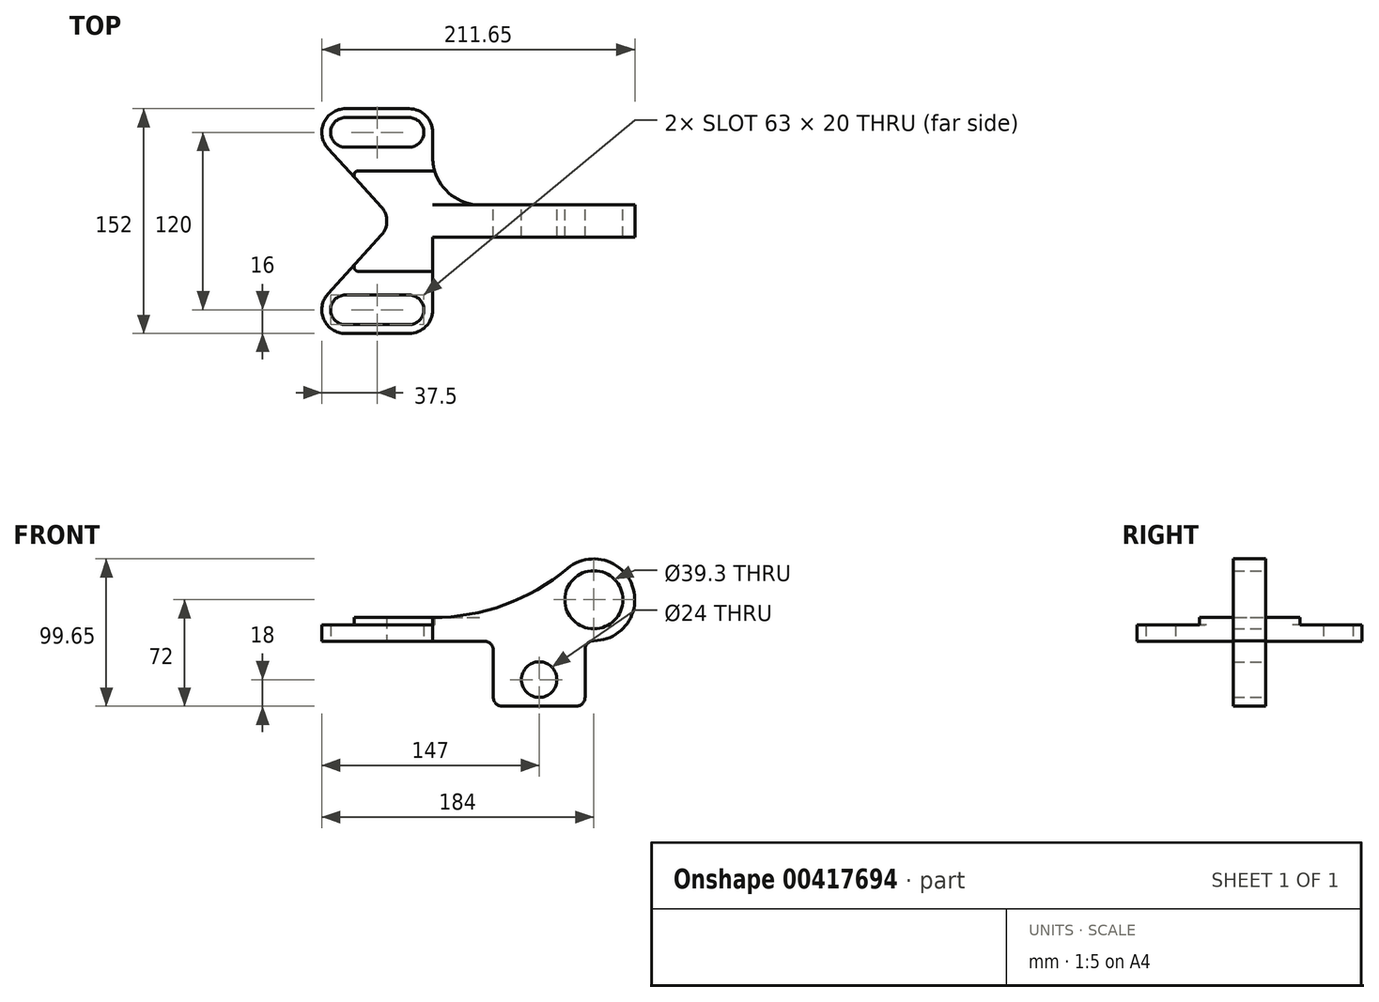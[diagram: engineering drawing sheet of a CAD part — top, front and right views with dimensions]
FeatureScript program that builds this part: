
annotation { "Feature Type Name" : "Feature", "Feature Type Description" : "" }
export const myFeature = defineFeature(function(context is Context, id is Id, definition is map)
    precondition{}
    {
        {
            var Q0;
            Q0=qCreatedBy(makeId("Top.planeOp"),FACE);
            var sketch = newSketch(context, id + "F0", { "sketchPlane" : qUnion([Q0])});
            skLineSegment(sketch, "E0.bottom", {"start": v(-59, 70) * mm, "end": v(-16, 70) * mm});
            skLineSegment(sketch, "E0.top", {"start": v(-59, 50) * mm, "end": v(-16, 50) * mm});
            skLineSegment(sketch, "E0.left", {"start": v(-59, 70) * mm, "end": v(-59, 50) * mm, "construction": true});
            skLineSegment(sketch, "E0.right", {"start": v(-16, 70) * mm, "end": v(-16, 50) * mm, "construction": true});
            skArc(sketch, "E1", {"start": v(-59, 70) * mm, "mid": v(-69, 60) * mm, "end": v(-59, 50) * mm});
            skArc(sketch, "E2", {"start": v(-16, 50) * mm, "mid": v(-6, 60) * mm, "end": v(-16, 70) * mm});
            skArc(sketch, "E3.0", {"start": v(-59, 76) * mm, "mid": v(-73.63, 66.47) * mm, "end": v(-70.84, 49.24) * mm});
            skLineSegment(sketch, "E3.1", {"start": v(-59, 76) * mm, "end": v(-16, 76) * mm});
            skArc(sketch, "E3.2", {"start": v(-16, 44) * mm, "mid": v(-4.69, 48.69) * mm, "end": v(0, 60) * mm, "construction": true});
            skLineSegment(sketch, "E3.3", {"start": v(-59, 44) * mm, "end": v(-16, 44) * mm, "construction": true});
            skLineSegment(sketch, "E4", {"start": v(-70.84, 49.24) * mm, "end": v(-34.64, 9.42) * mm});
            skLineSegment(sketch, "E5", {"start": v(0, 60) * mm, "end": v(0, 0) * mm});
            skArc(sketch, "E6", {"start": v(-31, 0) * mm, "mid": v(-31.94, 5.05) * mm, "end": v(-34.64, 9.42) * mm});
            skArc(sketch, "E7", {"start": v(-70.84, 49.24) * mm, "mid": v(-65.47, 45.37) * mm, "end": v(-59, 44) * mm, "construction": true});
            skArc(sketch, "E8", {"start": v(0, 60) * mm, "mid": v(-4.69, 71.31) * mm, "end": v(-16, 76) * mm});
            skArc(sketch, "E9.MirrorCS", {"start": v(-31, 0) * mm, "mid": v(-31.94, -5.05) * mm, "end": v(-34.64, -9.42) * mm});
            skLineSegment(sketch, "E10.MirrorCS", {"start": v(-70.84, -49.24) * mm, "end": v(-34.64, -9.42) * mm});
            skArc(sketch, "E11.MirrorCS", {"start": v(-59, -76) * mm, "mid": v(-73.63, -66.47) * mm, "end": v(-70.84, -49.24) * mm});
            skLineSegment(sketch, "E12.MirrorCS", {"start": v(-59, -76) * mm, "end": v(-16, -76) * mm});
            skArc(sketch, "E13.MirrorCS", {"start": v(0, -60) * mm, "mid": v(-4.69, -71.31) * mm, "end": v(-16, -76) * mm});
            skLineSegment(sketch, "E14.MirrorCS", {"start": v(0, -60) * mm, "end": v(0, 0) * mm});
            skArc(sketch, "E15.MirrorCS", {"start": v(-16, -50) * mm, "mid": v(-6, -60) * mm, "end": v(-16, -70) * mm});
            skLineSegment(sketch, "E16.MirrorCS", {"start": v(-59, -50) * mm, "end": v(-16, -50) * mm});
            skArc(sketch, "E17.MirrorCS", {"start": v(-59, -70) * mm, "mid": v(-69, -60) * mm, "end": v(-59, -50) * mm});
            skLineSegment(sketch, "E18.MirrorCS", {"start": v(-59, -70) * mm, "end": v(-16, -70) * mm});
            skSolve(sketch);
        }
        {
            var Q0;
            Q0=makeQuery(id+"F0.imprint","IMPRINT",FACE,{"disambiguationData":[TD([[makeQuery(id+"F0.imprint","IMPRINT",EDGE,{"derivedFrom":sQuery(id+"F0.wireOp",EDGE,"E0.bottom")}),1.0]])]});
            extrude(context, id + "F1", {"entities" : qUnion([Q0]), "depth" : 11 * mm});
        }
        {
            var Q0;
            Q0=makeQuery(id+"F1.opExtrude","CAP_FACE",FACE,{"disambiguationData":[OSD([sQuery(id+"F0.wireOp",EDGE,"E0.bottom"),sQuery(id+"F0.wireOp",EDGE,"E0.top"),sQuery(id+"F0.wireOp",EDGE,"E1"),sQuery(id+"F0.wireOp",EDGE,"E2"),sQuery(id+"F0.wireOp",EDGE,"E3.0"),sQuery(id+"F0.wireOp",EDGE,"E3.1"),sQuery(id+"F0.wireOp",EDGE,"E4"),sQuery(id+"F0.wireOp",EDGE,"E5"),sQuery(id+"F0.wireOp",EDGE,"E6"),sQuery(id+"F0.wireOp",EDGE,"E8"),sQuery(id+"F0.wireOp",EDGE,"E9.MirrorCS"),sQuery(id+"F0.wireOp",EDGE,"E10.MirrorCS"),sQuery(id+"F0.wireOp",EDGE,"E11.MirrorCS"),sQuery(id+"F0.wireOp",EDGE,"E12.MirrorCS"),sQuery(id+"F0.wireOp",EDGE,"E13.MirrorCS"),sQuery(id+"F0.wireOp",EDGE,"E14.MirrorCS"),sQuery(id+"F0.wireOp",EDGE,"E15.MirrorCS"),sQuery(id+"F0.wireOp",EDGE,"E16.MirrorCS"),sQuery(id+"F0.wireOp",EDGE,"E17.MirrorCS"),sQuery(id+"F0.wireOp",EDGE,"E18.MirrorCS")])],"isStart":false});
            var sketch = newSketch(context, id + "F2", { "sketchPlane" : qUnion([Q0])});
            skLineSegment(sketch, "E19.0", {"start": v(-52.43, 28.98) * mm, "end": v(-34.64, 9.42) * mm});
            skArc(sketch, "E19.1", {"start": v(-34.64, -9.42) * mm, "mid": v(-31, 0) * mm, "end": v(-34.64, 9.42) * mm});
            skLineSegment(sketch, "E19.2", {"start": v(-52.43, -28.98) * mm, "end": v(-34.64, -9.42) * mm});
            skLineSegment(sketch, "E19.3", {"start": v(0, 34) * mm, "end": v(0, -34) * mm});
            skLineSegment(sketch, "E20", {"start": v(-50.2, 34) * mm, "end": v(0, 34) * mm});
            skLineSegment(sketch, "E21.MirrorCS", {"start": v(-50.2, -34) * mm, "end": v(0, -34) * mm});
            skPoint(sketch, "E22.orphan", {"position": v(-70.84, 49.24) * mm});
            skPoint(sketch, "E23.orphan", {"position": v(0, 60) * mm});
            skPoint(sketch, "E24.orphan", {"position": v(0, -60) * mm});
            skPoint(sketch, "E25.orphan", {"position": v(-70.84, -49.24) * mm});
            skPoint(sketch, "E26.visualSharp", {"position": v(-56.99, 34) * mm});
            skArc(sketch, "E26.filletArc", {"start": v(-50.2, 34) * mm, "mid": v(-52.95, 32.21) * mm, "end": v(-52.43, 28.98) * mm});
            skPoint(sketch, "E27.visualSharp", {"position": v(-56.99, -34) * mm});
            skArc(sketch, "E27.filletArc", {"start": v(-52.43, -28.98) * mm, "mid": v(-52.95, -32.21) * mm, "end": v(-50.2, -34) * mm});
            skSolve(sketch);
        }
        {
            var Q0;
            Q0=makeQuery(id+"F2.imprint","IMPRINT",FACE,{"disambiguationData":[TD([[makeQuery(id+"F2.imprint","IMPRINT",EDGE,{"derivedFrom":sQuery(id+"F2.wireOp",EDGE,"E19.0")}),1.0]])]});
            extrude(context, id + "F3", {"entities" : qUnion([Q0]), "operationType" : NewBodyOperationType.ADD, "depth" : 5 * mm});
        }
        {
            var Q0;
            Q0=qCreatedBy(makeId("Front.planeOp"),FACE);
            var sketch = newSketch(context, id + "F4", { "sketchPlane" : qUnion([Q0])});
            skLineSegment(sketch, "E28", {"start": v(0, 0) * mm, "end": v(0, 16) * mm});
            skCircle(sketch, "E29", {"center": v(109, 28) * mm, "radius": 19.65 * mm});
            skCircle(sketch, "E30", {"center": v(72, -26) * mm, "radius": 12 * mm});
            skArc(sketch, "E31", {"start": v(0, 16) * mm, "mid": v(48.54, 24.55) * mm, "end": v(91.24, 49.19) * mm});
            skLineSegment(sketch, "E32", {"start": v(103, -5.65) * mm, "end": v(103, -38) * mm});
            skLineSegment(sketch, "E33", {"start": v(97, -44) * mm, "end": v(47, -44) * mm});
            skLineSegment(sketch, "E34", {"start": v(41, -38) * mm, "end": v(41, -6) * mm});
            skLineSegment(sketch, "E35", {"start": v(35, 0) * mm, "end": v(0, 0) * mm});
            skArc(sketch, "E36", {"start": v(109, 0.35) * mm, "mid": v(104.76, -1.4) * mm, "end": v(103, -5.65) * mm});
            skPoint(sketch, "E37.visualSharp", {"position": v(41, 0) * mm});
            skArc(sketch, "E37.filletArc", {"start": v(41, -6) * mm, "mid": v(39.24, -1.76) * mm, "end": v(35, 0) * mm});
            skPoint(sketch, "E38.visualSharp", {"position": v(41, -44) * mm});
            skArc(sketch, "E38.filletArc", {"start": v(41, -38) * mm, "mid": v(42.76, -42.24) * mm, "end": v(47, -44) * mm});
            skPoint(sketch, "E39.visualSharp", {"position": v(103, -44) * mm});
            skArc(sketch, "E39.filletArc", {"start": v(97, -44) * mm, "mid": v(101.24, -42.24) * mm, "end": v(103, -38) * mm});
            skArc(sketch, "E40", {"start": v(91.24, 49.19) * mm, "mid": v(83.02, 18.55) * mm, "end": v(109, 0.35) * mm, "construction": true});
            skArc(sketch, "E41", {"start": v(109, 0.35) * mm, "mid": v(134.98, 37.45) * mm, "end": v(91.24, 49.19) * mm});
            skLineSegment(sketch, "E42.0", {"start": v(-50.2, 16) * mm, "end": v(0, 16) * mm, "construction": true});
            skSolve(sketch);
        }
        {
            var Q0;
            Q0=makeQuery(id+"F4.imprint","IMPRINT",FACE,{"disambiguationData":[TD([[makeQuery(id+"F4.imprint","IMPRINT",EDGE,{"derivedFrom":sQuery(id+"F4.wireOp",EDGE,"E28")}),-1.0]])]});
            extrude(context, id + "F5", {"entities" : qUnion([Q0]), "operationType" : NewBodyOperationType.ADD, "endBound" : BoundingType.SYMMETRIC, "depth" : 22 * mm});
        }
        {
            var Q0;
            Q0=qCreatedBy(makeId("Top.planeOp"),FACE);
            var sketch = newSketch(context, id + "F6", { "sketchPlane" : qUnion([Q0])});
            skArc(sketch, "E43", {"start": v(0, 43) * mm, "mid": v(9.37, 20.37) * mm, "end": v(32, 11) * mm});
            skLineSegment(sketch, "E44.0", {"start": v(0, 34) * mm, "end": v(0, 11) * mm});
            skLineSegment(sketch, "E44.1", {"start": v(0, 11) * mm, "end": v(32, 11) * mm});
            skLineSegment(sketch, "E44.2", {"start": v(0, 43) * mm, "end": v(0, 34) * mm});
            skPoint(sketch, "E45.orphan", {"position": v(0, 60) * mm});
            skPoint(sketch, "E46.orphan", {"position": v(91.24, 11) * mm});
            skArc(sketch, "E47.MirrorCS", {"start": v(0, -43) * mm, "mid": v(9.37, -20.37) * mm, "end": v(32, -11) * mm});
            skLineSegment(sketch, "E48.MirrorCS", {"start": v(0, -11) * mm, "end": v(32, -11) * mm});
            skLineSegment(sketch, "E49.MirrorCS", {"start": v(0, -34) * mm, "end": v(0, -11) * mm});
            skLineSegment(sketch, "E50.MirrorCS", {"start": v(0, -43) * mm, "end": v(0, -34) * mm});
            skSolve(sketch);
        }
        {
            var Q0;
            Q0=makeQuery(id+"F6.imprint","IMPRINT",FACE,{"disambiguationData":[TD([[makeQuery(id+"F6.imprint","IMPRINT",EDGE,{"derivedFrom":sQuery(id+"F6.wireOp",EDGE,"E43")}),-1.0]])]});
            var Q1;
            Q1=makeQuery(id+"F6.imprint","IMPRINT",FACE,{"disambiguationData":[TD([[makeQuery(id+"F6.imprint","IMPRINT",EDGE,{"derivedFrom":sQuery(id+"F6.wireOp",EDGE,"E47.MirrorCS")}),1.0]])]});
            var Q2;
            Q2=makeQuery(id+"F3.opExtrude","CAP_FACE",FACE,{"disambiguationData":[OSD([sQuery(id+"F2.wireOp",EDGE,"E19.0"),sQuery(id+"F2.wireOp",EDGE,"E19.1"),sQuery(id+"F2.wireOp",EDGE,"E19.2"),sQuery(id+"F2.wireOp",EDGE,"E19.3"),sQuery(id+"F2.wireOp",EDGE,"E20"),sQuery(id+"F2.wireOp",EDGE,"E21.MirrorCS"),sQuery(id+"F2.wireOp",EDGE,"E26.filletArc"),sQuery(id+"F2.wireOp",EDGE,"E27.filletArc")])],"isStart":false});
            extrude(context, id + "F7", {"entities" : qUnion([Q0, Q1]), "operationType" : NewBodyOperationType.ADD, "endBound" : BoundingType.UP_TO_SURFACE, "endBoundEntityFace" : qUnion([Q2]), "depth" : 25 * mm});
        }
        {
            var Q0;
            Q0=qCreatedBy(makeId("Right.planeOp"),FACE);
            var sketch = newSketch(context, id + "F8", { "sketchPlane" : qUnion([Q0])});
            skLineSegment(sketch, "E51.bottom", {"start": v(43, 16) * mm, "end": v(34, 16) * mm});
            skLineSegment(sketch, "E51.top", {"start": v(43, 11) * mm, "end": v(34, 11) * mm});
            skLineSegment(sketch, "E51.left", {"start": v(43, 16) * mm, "end": v(43, 11) * mm});
            skLineSegment(sketch, "E51.right", {"start": v(34, 16) * mm, "end": v(34, 11) * mm});
            skLineSegment(sketch, "E52.MirrorCS", {"start": v(-34, 16) * mm, "end": v(-34, 11) * mm});
            skLineSegment(sketch, "E53.MirrorCS", {"start": v(-43, 16) * mm, "end": v(-43, 11) * mm});
            skLineSegment(sketch, "E54.MirrorCS", {"start": v(-43, 11) * mm, "end": v(-34, 11) * mm});
            skLineSegment(sketch, "E55.MirrorCS", {"start": v(-43, 16) * mm, "end": v(-34, 16) * mm});
            skSolve(sketch);
        }
        {
            var Q0;
            Q0=makeQuery(id+"F8.imprint","IMPRINT",FACE,{"disambiguationData":[TD([[makeQuery(id+"F8.imprint","IMPRINT",EDGE,{"derivedFrom":sQuery(id+"F8.wireOp",EDGE,"E51.bottom")}),1.0]])]});
            var Q1;
            Q1=makeQuery(id+"F8.imprint","IMPRINT",FACE,{"disambiguationData":[TD([[makeQuery(id+"F8.imprint","IMPRINT",EDGE,{"derivedFrom":sQuery(id+"F8.wireOp",EDGE,"E52.MirrorCS")}),-1.0]])]});
            extrude(context, id + "F9", {"entities" : qUnion([Q0, Q1]), "operationType" : NewBodyOperationType.REMOVE, "endBound" : BoundingType.THROUGH_ALL, "depth" : 25 * mm});
        }
    });
